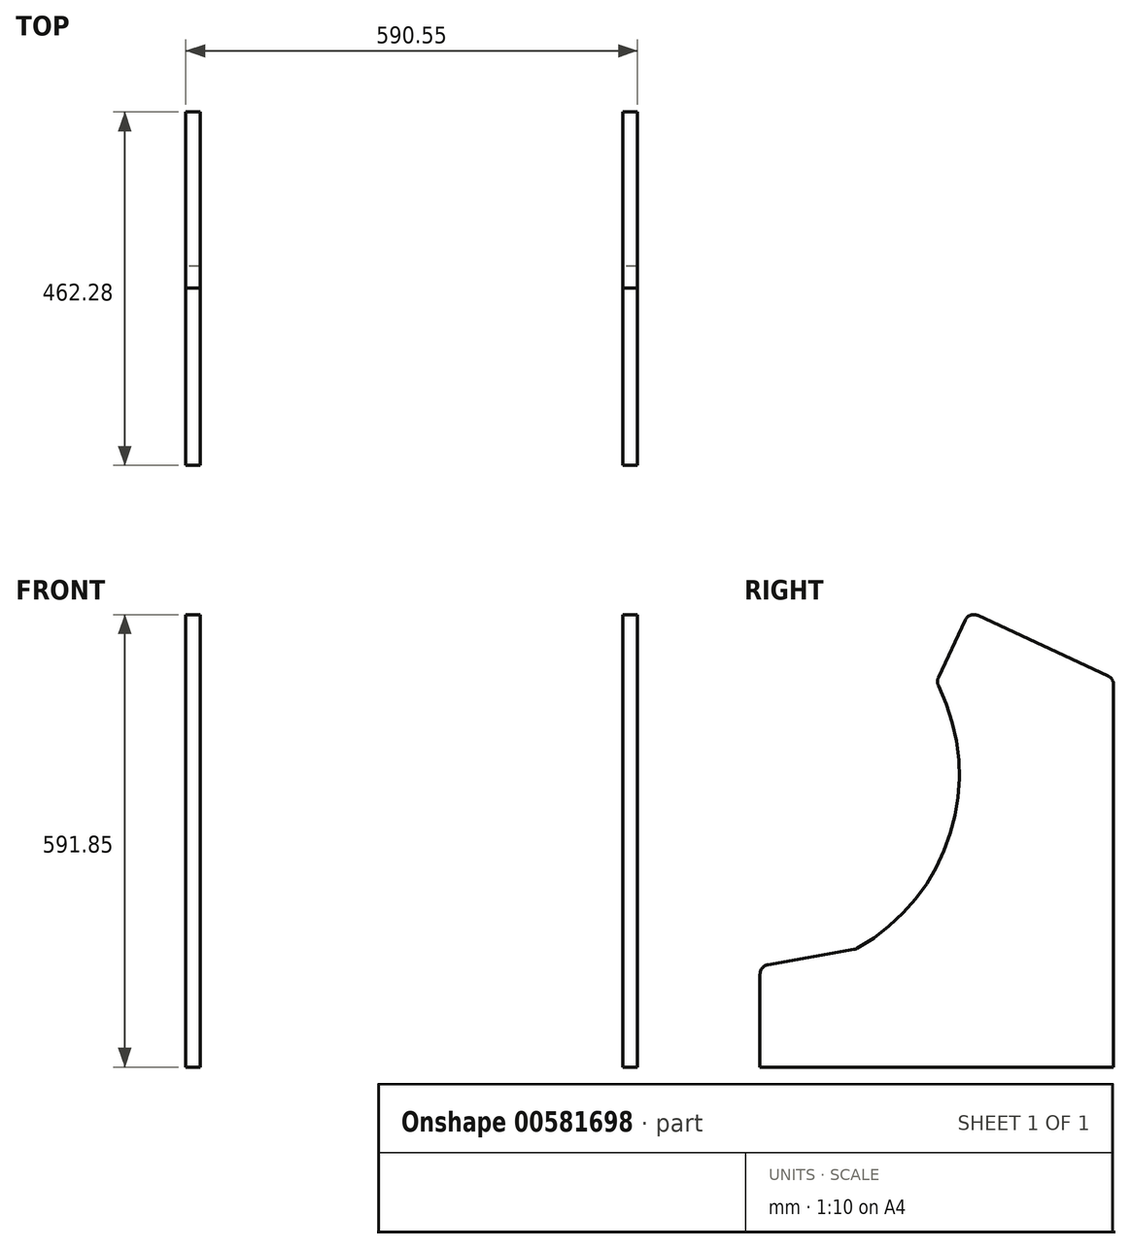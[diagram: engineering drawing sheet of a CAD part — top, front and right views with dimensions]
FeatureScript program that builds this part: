
annotation { "Feature Type Name" : "Feature", "Feature Type Description" : "" }
export const myFeature = defineFeature(function(context is Context, id is Id, definition is map)
    precondition{}
    {
        {
            var Q0;
            Q0=qCreatedBy(makeId("Right.planeOp"),FACE);
            var sketch = newSketch(context, id + "F0", { "sketchPlane" : qUnion([Q0])});
            skLineSegment(sketch, "E0", {"start": v(0, 499.9) * mm, "end": v(0, 0) * mm});
            skLineSegment(sketch, "E1.MirrorCS", {"start": v(-194.13, 584.51) * mm, "end": v(-229.08, 509.56) * mm});
            skLineSegment(sketch, "E2.MirrorCS", {"start": v(-462.28, 596.02) * mm, "end": v(-462.28, 132.08) * mm, "construction": true});
            skLineSegment(sketch, "E3.MirrorCS", {"start": v(-188.77, 596.02) * mm, "end": v(-462.28, 596.02) * mm, "construction": true});
            skLineSegment(sketch, "E4.MirrorCS", {"start": v(-7.33, 511.42) * mm, "end": v(-177.26, 590.66) * mm});
            skLineSegment(sketch, "E5", {"start": v(0, 0) * mm, "end": v(-462.28, 0) * mm});
            skLineSegment(sketch, "E6", {"start": v(-462.28, 0) * mm, "end": v(-462.28, 121.42) * mm});
            skLineSegment(sketch, "E7", {"start": v(-231.7, 503.94) * mm, "end": v(-231.7, 596.02) * mm, "construction": true});
            skLineSegment(sketch, "E8", {"start": v(-451.79, 133.93) * mm, "end": v(-339.3, 153.77) * mm});
            skArc(sketch, "E9", {"start": v(-335.3, 155.18) * mm, "mid": v(-213.42, 305.58) * mm, "end": v(-228.95, 498.55) * mm});
            skPoint(sketch, "E10.visualSharp", {"position": v(-462.28, 132.08) * mm});
            skArc(sketch, "E10.filletArc", {"start": v(-451.79, 133.93) * mm, "mid": v(-459.3, 129.59) * mm, "end": v(-462.28, 121.42) * mm});
            skPoint(sketch, "E11.visualSharp", {"position": v(-337.2, 154.13) * mm});
            skArc(sketch, "E11.filletArc", {"start": v(-339.3, 153.77) * mm, "mid": v(-337.24, 154.3) * mm, "end": v(-335.3, 155.18) * mm});
            skPoint(sketch, "E12.visualSharp", {"position": v(-231.7, 503.94) * mm});
            skArc(sketch, "E12.filletArc", {"start": v(-229.08, 509.56) * mm, "mid": v(-230.27, 504.04) * mm, "end": v(-228.95, 498.55) * mm});
            skPoint(sketch, "E13.visualSharp", {"position": v(-188.77, 596.02) * mm});
            skArc(sketch, "E13.filletArc", {"start": v(-177.26, 590.66) * mm, "mid": v(-186.97, 591.08) * mm, "end": v(-194.13, 584.51) * mm});
            skPoint(sketch, "E14.visualSharp", {"position": v(0, 508) * mm});
            skArc(sketch, "E14.filletArc", {"start": v(0, 499.9) * mm, "mid": v(-1.99, 506.73) * mm, "end": v(-7.33, 511.42) * mm});
            skSolve(sketch);
        }
        {
            var Q0;
            Q0=qSketchRegion(id+"F0",true);
            extrude(context, id + "F1", {"entities" : qUnion([Q0]), "depth" : 19.05 * mm});
        }
        {
            var Q0;
            Q0=makeQuery(id+"F1.opExtrude","SWEPT_BODY",BODY,{"disambiguationData":[OSD([sQuery(id+"F0.wireOp",EDGE,"E0"),sQuery(id+"F0.wireOp",EDGE,"E1.MirrorCS"),sQuery(id+"F0.wireOp",EDGE,"E4.MirrorCS"),sQuery(id+"F0.wireOp",EDGE,"E5"),sQuery(id+"F0.wireOp",EDGE,"E6"),sQuery(id+"F0.wireOp",EDGE,"6ce56614-1373-4aa3-ab08-7f8a37f793d1")])]});
            transform(context, id + "F2", {"entities" : qUnion([Q0]), "transformType" : TransformType.TRANSLATION_3D, "dx" : 571.5 * mm, "dy" : 0 * mm, "dz" : 0 * mm, "makeCopy" : true});
        }
    });
